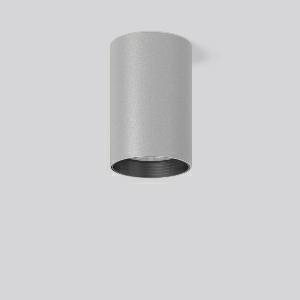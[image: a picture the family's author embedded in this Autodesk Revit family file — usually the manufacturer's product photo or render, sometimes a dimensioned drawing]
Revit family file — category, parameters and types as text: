
# Revit family: heledon_maxi_a_931234_004_f2a8
name_source: partatom
category: Lighting Fixtures
units: mm (PartAtom-declared; Revit-internal decimal feet)

## family parameters
Cut with Voids When Loaded = No
Host = Face
Light Source = No
Part Type = Normal
Room Calculation Point = No
Round Connector Dimension = Use Diameter
Shared = No

## types (1)
- HELEDON maxi A (1 x LED Modul 932 fresh meat, 1800 lm, 3200)
    Apparent Load = 33 VA
    Approval mark = CE
    CIE Flux Codes = 97 100 100 100 100
    Color Rendering = 90
    Color Temperature = 3200
    Default Elevation = 1800 mm  [stored 5.90551 ft]
    Description = Series: HELEDON maxi
Cylindrical surface-mounted downlight. Housing: die-cast aluminium, powder-coated. Internal ceiling frame polycarbonate with bayonet mounting. Black plastic ring and recessed LED to prevent glare from the side. Optical assembly with lens made of plastic (polycarbonate) for the best homogeneous light distribution - can be changed without tools. Special LED for illumination of meat included. Suitable for Ceiling mounting. Easy installation with a separate ceiling frame with bayonet mounting and plug connection. Driver integrated. Connected via plug-in connector. High quality converter without flickering and stroboscopic effect. The following accessories can be mounted without use of tools: interchangeable lenses, decorative glasses, honeycomb louvre, clear and frosted diffusers, white interchangeable plastic ring. 
Colour: silver
Diameter: 123 mm
Height: 183 mm
Lamp: LED
Socket: without socket
Colour temperature: fresh meat
System power: 33 W
Rated luminous flux: 1800 lm
Luminous efficiency: 55 lm/W
Control gear: Regulated power supply
Protection class: I
Type of protection: IP 20
    Height = 183 mm
    Lamp = 1 x LED Modul 932 fresh meat
    Lamp Light Flux = 1800 lm
    Lamp count = 1
    Length = 123 mm
    Lifetime = 50000 h
    Luminous efficacy = 55 lm/W
    Manufacturer = RZB
    ModVariant = No
    Model = 931234.004
    Mounting Place = Ceiling
    Mounting Type = Surface mounted
    Number of Poles = 1
    OnlyDefault = Yes
    Power Factor = 1
    Product Name = HELEDON maxi A
    Product group = Surface mounted downlights
    ProductGroupID = 302
    Protection Class = Protection class I
    Protection Degree = IP 20
    RLX_Detail_Level = 1
    RLX_Emergency_Light_Flux = 0 lm
    RLX_Emergency_Type = 0
    RLX_Emergency_Type_DB = No
    RlxData = <blob elided: 97077 chars, md5=dcf6b259>
    Socket = socket
    Standby Power = 0 W
    System Light Flux = 1800 lm
    System Power = 33 W
    Type Comments = Product without accessories
    Type Image = 931193.004.jpg
    URL = http://relux.com
    VarID = ---
    Voltage = 230 V
    Voltage Range = 220-240 V
    Weight = 0.00 kg
    Width = 0 mm  [stored 0 ft]

note: [stored X ft] marks values corroborated as IEEE doubles in the binary element streams (Revit-internal decimal feet)

## geometry (parser evidence)
native form markers: Blend x4, Sweep x10
no freeform markers — native parametric forms only
